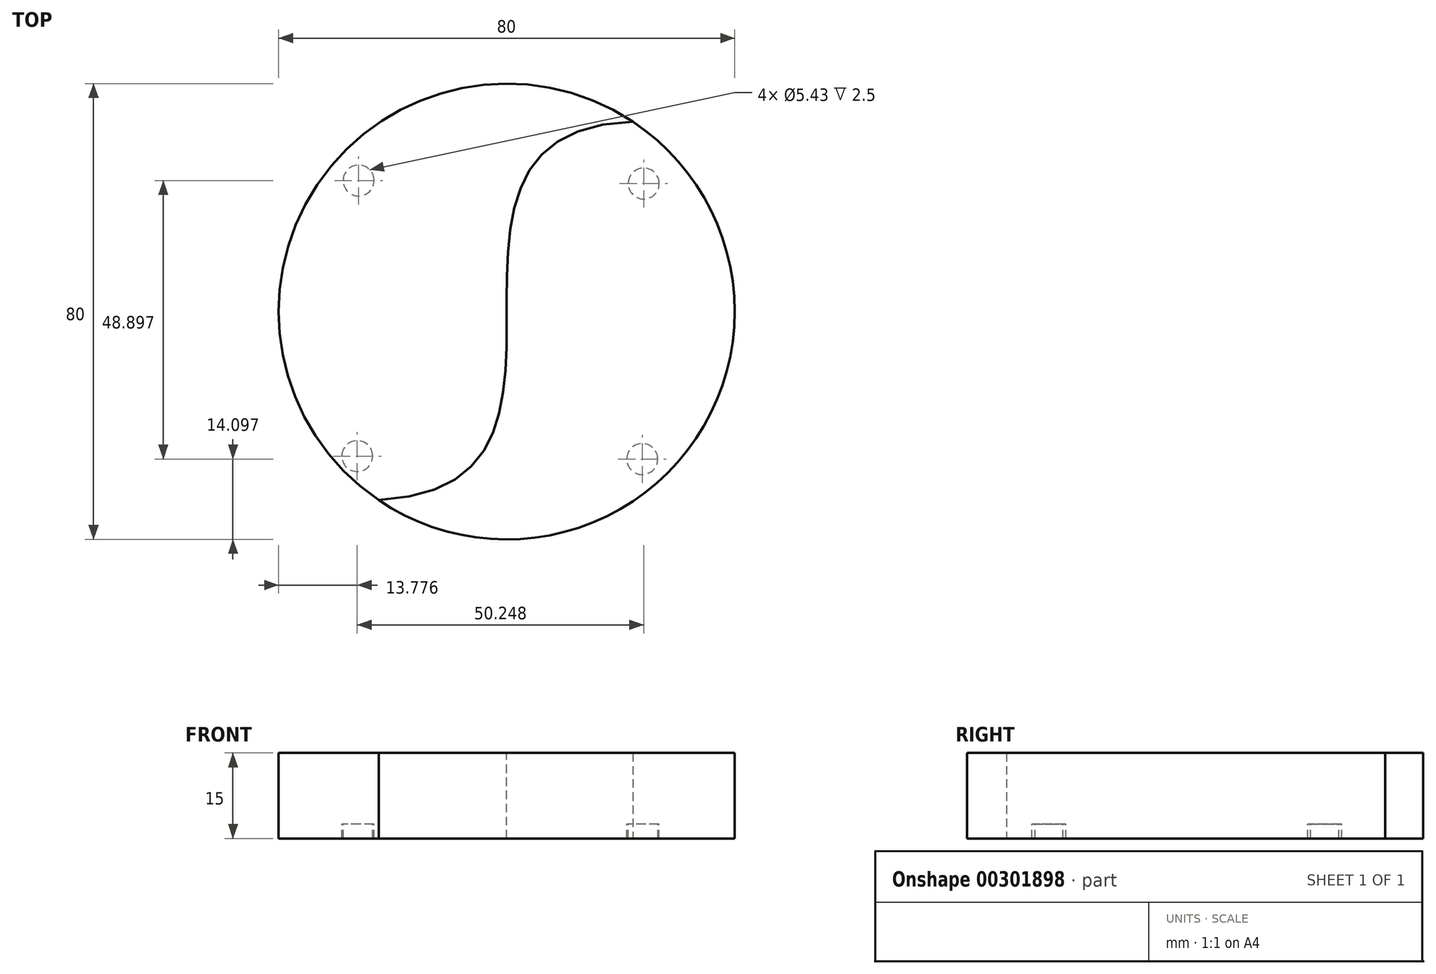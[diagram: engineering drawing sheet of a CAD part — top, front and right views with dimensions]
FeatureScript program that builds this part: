
annotation { "Feature Type Name" : "Feature", "Feature Type Description" : "" }
export const myFeature = defineFeature(function(context is Context, id is Id, definition is map)
    precondition{}
    {
        {
            var Q0;
            Q0=qCreatedBy(makeId("Top.planeOp"),FACE);
            var sketch = newSketch(context, id + "F0", { "sketchPlane" : qUnion([Q0])});
            skCircle(sketch, "E0", {"center": v(0, 0) * mm, "radius": 40 * mm});
            skFitSpline(sketch, "E1", {"points": [v(22.14, 33.31) * mm, v(0, 0) * mm, v(-22.46, -33.1) * mm], "startDerivative": vector(-132.84, -3.76) * mm, "endDerivative": vector(-134.74, -7.14) * mm});
            skSolve(sketch);
        }
        {
            var Q0;
            {var subQ0=sQuery(id+"F0.wireOp",EDGE,"E1");Q0=makeQuery(id+"F0.imprint","IMPRINT",FACE,{"disambiguationData":[TD([[makeQuery(id+"F0.imprint","IMPRINT",EDGE,{"derivedFrom":subQ0}),1.0]])]});}
            extrude(context, id + "F1", {"entities" : qUnion([Q0]), "depth" : 15 * mm});
        }
        {
            var Q0;
            {var subQ0=sQuery(id+"F0.wireOp",EDGE,"E1");Q0=makeQuery(id+"F0.imprint","IMPRINT",FACE,{"disambiguationData":[TD([[makeQuery(id+"F0.imprint","IMPRINT",EDGE,{"derivedFrom":subQ0}),-1.0]])]});}
            extrude(context, id + "F2", {"entities" : qUnion([Q0]), "depth" : 15 * mm});
        }
        {
            var Q0;
            Q0=qCreatedBy(makeId("Top.planeOp"),FACE);
            var sketch = newSketch(context, id + "F3", { "sketchPlane" : qUnion([Q0])});
            skCircle(sketch, "E2", {"center": v(-25.98, 23) * mm, "radius": 2.72 * mm});
            skCircle(sketch, "E3", {"center": v(-26.22, -25.38) * mm, "radius": 2.72 * mm});
            skCircle(sketch, "E4", {"center": v(23.78, -25.9) * mm, "radius": 2.72 * mm});
            skCircle(sketch, "E5", {"center": v(24.02, 22.47) * mm, "radius": 2.72 * mm});
            skSolve(sketch);
        }
        {
            var Q0;
            Q0=makeQuery(id+"F3.imprint","IMPRINT",FACE,{"disambiguationData":[TD([[makeQuery(id+"F3.imprint","IMPRINT",EDGE,{"derivedFrom":sQuery(id+"F3.wireOp",EDGE,"E2")}),1.0]])]});
            var Q1;
            Q1=makeQuery(id+"F3.imprint","IMPRINT",FACE,{"disambiguationData":[TD([[makeQuery(id+"F3.imprint","IMPRINT",EDGE,{"derivedFrom":sQuery(id+"F3.wireOp",EDGE,"E3")}),1.0]])]});
            var Q2;
            Q2=makeQuery(id+"F3.imprint","IMPRINT",FACE,{"disambiguationData":[TD([[makeQuery(id+"F3.imprint","IMPRINT",EDGE,{"derivedFrom":sQuery(id+"F3.wireOp",EDGE,"E5")}),1.0]])]});
            var Q3;
            Q3=makeQuery(id+"F3.imprint","IMPRINT",FACE,{"disambiguationData":[TD([[makeQuery(id+"F3.imprint","IMPRINT",EDGE,{"derivedFrom":sQuery(id+"F3.wireOp",EDGE,"E4")}),1.0]])]});
            extrude(context, id + "F4", {"entities" : qUnion([Q0, Q1, Q2, Q3]), "operationType" : NewBodyOperationType.REMOVE, "oppositeDirection" : true, "depth" : 5 * mm, "symmetric" : true});
        }
    });
